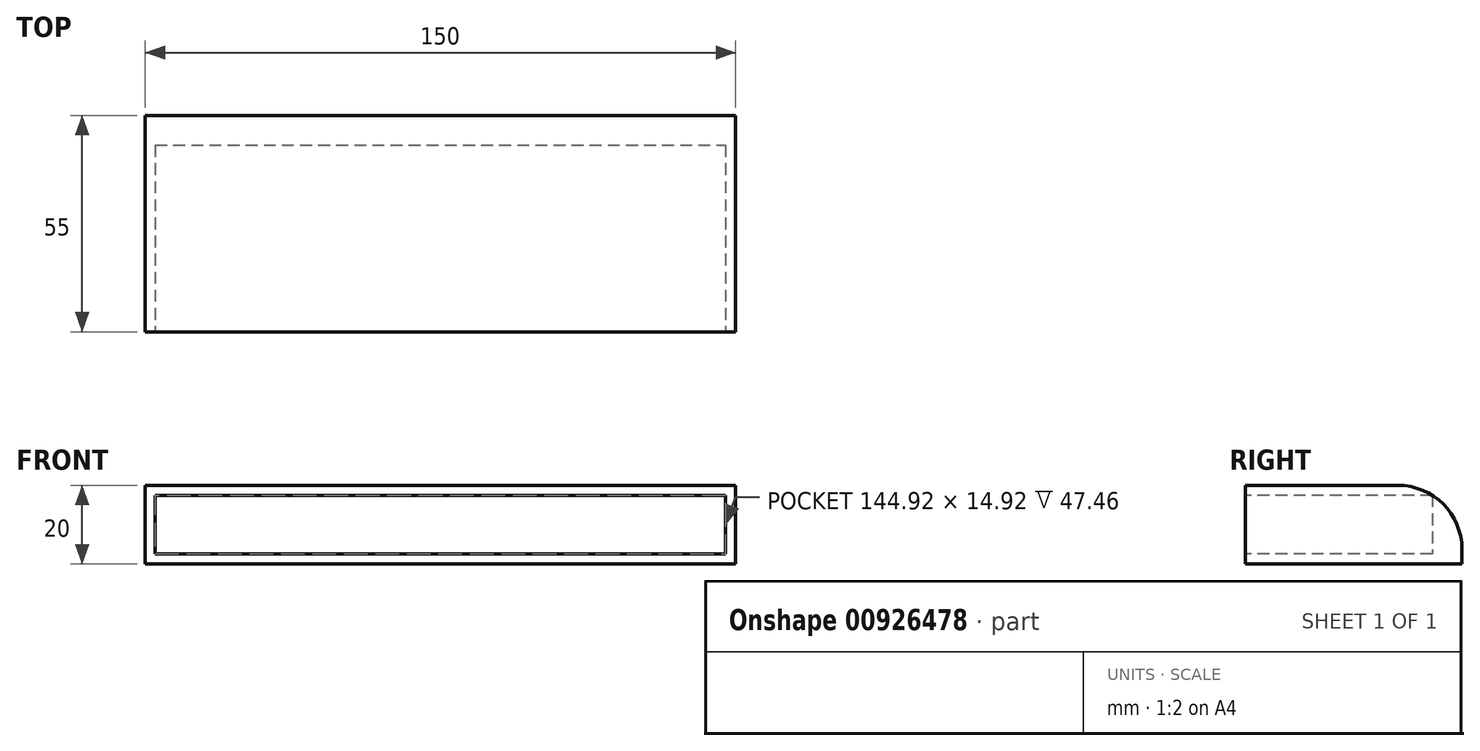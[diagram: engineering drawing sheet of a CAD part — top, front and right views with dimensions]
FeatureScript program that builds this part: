
annotation { "Feature Type Name" : "Feature", "Feature Type Description" : "" }
export const myFeature = defineFeature(function(context is Context, id is Id, definition is map)
    precondition{}
    {
        {
            var Q0;
            Q0=qCreatedBy(makeId("Top.planeOp"),FACE);
            var sketch = newSketch(context, id + "F0", { "sketchPlane" : qUnion([Q0])});
            skLineSegment(sketch, "E0.bottom", {"start": v(-73.35, 16.52) * mm, "end": v(76.65, 16.52) * mm});
            skLineSegment(sketch, "E0.top", {"start": v(-73.35, -33.48) * mm, "end": v(76.65, -33.48) * mm});
            skLineSegment(sketch, "E0.left", {"start": v(-73.35, 16.52) * mm, "end": v(-73.35, -33.48) * mm});
            skLineSegment(sketch, "E0.right", {"start": v(76.65, 16.52) * mm, "end": v(76.65, -33.48) * mm});
            skSolve(sketch);
        }
        {
            var Q0;
            Q0=makeQuery(id+"F0.imprint","IMPRINT",FACE,{"disambiguationData":[TD([[makeQuery(id+"F0.imprint","IMPRINT",EDGE,{"derivedFrom":sQuery(id+"F0.wireOp",EDGE,"E0.bottom")}),-1.0]])]});
            extrude(context, id + "F1", {"entities" : qUnion([Q0]), "depth" : 20 * mm, "offsetDistance" : 25.4 * mm});
        }
        {
            var Q0;
            Q0=makeQuery(id+"F1.opExtrude","SWEPT_FACE",FACE,{"disambiguationData":[OSD([sQuery(id+"F0.wireOp",EDGE,"E0.top")])]});
            shell(context, id + "F2", {"entities" : qUnion([Q0]), "thickness" : 2.54 * mm});
        }
        {
            var Q0;
            Q0=makeQuery(id+"F1.opExtrude","SWEPT_FACE",FACE,{"disambiguationData":[OSD([sQuery(id+"F0.wireOp",EDGE,"E0.bottom")])]});
            extrude(context, id + "F3", {"entities" : qUnion([Q0]), "operationType" : NewBodyOperationType.ADD, "depth" : 5 * mm, "offsetDistance" : 25.4 * mm});
        }
        {
            var Q0;
            {var subQ0=sQuery(id+"F0.wireOp",EDGE,"E0.bottom");Q0=makeQuery(id+"F3.opExtrude","CAP_EDGE",EDGE,{"disambiguationData":[OSD([subQ0]),TDD([makeQuery(id+"F1.opExtrude","CAP_EDGE",EDGE,{"disambiguationData":[OSD([subQ0])],"isStart":false})])],"isStart":false});}
            fillet(context, id + "F4", {"entities" : qUnion([Q0]), "radius" : 16.26 * mm, "tangentPropagation" : true, "allowEdgeOverflow" : false});
        }
    });
